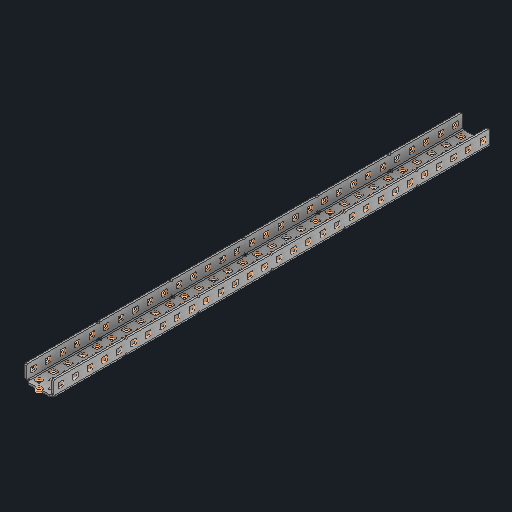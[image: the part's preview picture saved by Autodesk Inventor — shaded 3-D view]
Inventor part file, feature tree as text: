
AUTODESK INVENTOR PART (.ipt)
format: ipt  version: 2025 (Build 290162000, 162)  size: 2,424,832 bytes
history: native  units: in
note: dims shown in document units (in); Inventor stores cm internally (conversion verified against a paired STEP export)
features: other x306, sketch x5, sheet_metal_op x1
ambient origin geometry x8: Origin, YZ Plane, XZ Plane, XY Plane, X Axis, Y Axis, Z Axis, Center Point
bodies: Solid1 (feature_tree)
feature tree (312):
  other  "Alu C 1x2x1x30.ipt"
  other  "Solid1::Alu C 1x2x1x30.ipt"
  other  "TaggingFeature1"
  sketch  "Sketch1"  dims[d0=0.3937in]
  sketch  "Sketch2"  dims[d1=0.0625in]
  sketch  "Sketch3"
  other  "Flange Pattern Sketch"
  sketch  "Sketch9"
  sheet_metal_op  "Body Pattern Sketch"
  other  "Arc Length"
  sketch  "Sketch14"
  other  "Flange Pattern Plane"
  other  "Srf1"
  other  "Srf2"
  other  "Srf3"
  other  "Srf4"
  other  "Srf5"
  other  "Srf6"
  other  "Srf7"
  other  "Srf8"
  other  "Srf9"
  other  "Srf10"
  other  "Srf11"
  other  "Srf12"
  other  "Srf13"
  other  "Srf14"
  other  "Srf15"
  other  "Srf16"
  other  "Srf17"
  other  "Srf18"
  other  "Srf19"
  other  "Srf20"
  other  "Srf21"
  other  "Srf22"
  other  "Srf23"
  other  "Srf24"
  other  "Srf25"
  other  "Srf26"
  other  "Srf27"
  other  "Srf28"
  other  "Srf29"
  other  "Srf30"
  other  "Srf31"
  other  "Srf32"
  other  "Srf33"
  other  "Srf34"
  other  "Srf35"
  other  "Srf36"
  other  "Srf37"
  other  "Srf38"
  other  "Srf39"
  other  "Srf40"
  other  "Srf41"
  other  "Srf42"
  other  "Srf43"
  other  "Srf44"
  other  "Srf45"
  other  "Srf46"
  other  "Srf47"
  other  "Srf48"
  other  "Srf49"
  other  "Srf50"
  other  "Srf51"
  other  "Srf52"
  other  "Srf53"
  other  "Srf54"
  other  "Srf55"
  other  "Srf56"
  other  "Srf57"
  other  "Srf58"
  other  "Srf59"
  other  "Srf60"
  other  "Srf61"
  other  "Srf62"
  other  "Srf63"
  other  "Srf64"
  other  "Srf65"
  other  "Srf66"
  other  "Srf67"
  other  "Srf68"
  other  "Srf69"
  other  "Srf70"
  other  "Srf71"
  other  "Srf72"
  other  "Srf73"
  other  "Srf74"
  other  "Srf75"
  other  "Srf76"
  other  "Srf77"
  other  "Srf78"
  other  "Srf79"
  other  "Srf80"
  other  "Srf81"
  other  "Srf82"
  other  "Srf83"
  other  "Srf84"
  other  "Srf85"
  other  "Srf86"
  other  "Srf87"
  other  "Srf88"
  other  "Srf89"
  other  "Srf90"
  other  "Srf91"
  other  "Srf92"
  other  "Srf93"
  other  "Srf94"
  other  "Srf95"
  other  "Srf96"
  other  "Srf97"
  other  "Srf98"
  other  "Srf99"
  other  "Srf100"
  other  "Srf101"
  other  "Srf102"
  other  "Srf103"
  other  "Srf104"
  other  "Srf105"
  other  "Srf106"
  other  "Srf107"
  other  "Srf108"
  other  "Srf109"
  other  "Srf110"
  other  "Srf111"
  other  "Srf112"
  other  "Srf113"
  other  "Srf114"
  other  "Srf115"
  other  "Srf116"
  other  "Srf117"
  other  "Srf118"
  other  "Srf119"
  other  "Srf120"
  other  "Srf121"
  other  "Srf122"
  other  "Srf123"
  other  "Srf124"
  other  "Srf125"
  other  "Srf126"
  other  "Srf127"
  other  "Srf128"
  other  "Srf129"
  other  "Srf130"
  other  "Srf131"
  other  "Srf132"
  other  "Srf133"
  other  "Srf134"
  other  "Srf135"
  other  "Srf136"
  other  "Srf137"
  other  "Srf138"
  other  "Srf139"
  other  "Srf140"
  other  "Srf141"
  other  "Srf142"
  other  "Srf143"
  other  "Srf144"
  other  "Srf145"
  other  "Srf146"
  other  "Srf147"
  other  "Srf148"
  other  "Srf149"
  other  "Srf150"
  other  "Srf1::Derived"
  other  "Srf2::Derived"
  other  "Srf823::Derived"
  other  "Srf824::Derived"
  other  "Srf825::Derived"
  other  "Srf826::Derived"
  other  "Srf827::Derived"
  other  "Srf828::Derived"
  other  "Srf829::Derived"
  other  "Srf922::Derived"
  other  "Srf923::Derived"
  other  "Srf924::Derived"
  other  "Srf925::Derived"
  other  "Srf926::Derived"
  other  "Srf1143::Derived"
  other  "Srf1144::Derived"
  other  "Srf1145::Derived"
  other  "Srf1146::Derived"
  other  "Srf1147::Derived"
  other  "Srf1148::Derived"
  other  "Srf1149::Derived"
  other  "Srf1150::Derived"
  other  "Srf1151::Derived"
  other  "Srf1152::Derived"
  other  "Srf1153::Derived"
  other  "Srf1154::Derived"
  other  "Srf1155::Derived"
  other  "Srf1156::Derived"
  other  "Srf1157::Derived"
  other  "Srf1158::Derived"
  other  "Srf1159::Derived"
  other  "Srf1160::Derived"
  other  "Srf1161::Derived"
  other  "Srf1162::Derived"
  other  "Srf1163::Derived"
  other  "Srf1164::Derived"
  other  "Srf1165::Derived"
  other  "Srf1166::Derived"
  other  "Srf1167::Derived"
  other  "Srf1168::Derived"
  other  "Srf1169::Derived"
  other  "Srf1170::Derived"
  other  "Srf1171::Derived"
  other  "Srf1172::Derived"
  other  "Srf1173::Derived"
  other  "Srf1174::Derived"
  other  "Srf1175::Derived"
  other  "Srf1176::Derived"
  other  "Srf1177::Derived"
  other  "Srf1178::Derived"
  other  "Srf1179::Derived"
  other  "Srf1180::Derived"
  other  "Srf1181::Derived"
  other  "Srf1182::Derived"
  other  "Srf1183::Derived"
  other  "Srf1184::Derived"
  other  "Srf1185::Derived"
  other  "Srf1186::Derived"
  other  "Srf1187::Derived"
  other  "Srf1188::Derived"
  other  "Srf91::Derived"
  other  "Srf92::Derived"
  other  "Srf856::Derived"
  other  "Srf857::Derived"
  other  "Srf858::Derived"
  other  "Srf859::Derived"
  other  "Srf860::Derived"
  other  "Srf861::Derived"
  other  "Srf862::Derived"
  other  "Srf959::Derived"
  other  "Srf960::Derived"
  other  "Srf961::Derived"
  other  "Srf962::Derived"
  other  "Srf963::Derived"
  other  "Srf1199::Derived"
  other  "Srf1200::Derived"
  other  "Srf1201::Derived"
  other  "Srf1202::Derived"
  other  "Srf1203::Derived"
  other  "Srf1204::Derived"
  other  "Srf1205::Derived"
  other  "Srf1206::Derived"
  other  "Srf1207::Derived"
  other  "Srf1208::Derived"
  other  "Srf1209::Derived"
  other  "Srf1210::Derived"
  other  "Srf1211::Derived"
  other  "Srf1212::Derived"
  other  "Srf1213::Derived"
  other  "Srf1214::Derived"
  other  "Srf1215::Derived"
  other  "Srf1216::Derived"
  other  "Srf1217::Derived"
  other  "Srf1218::Derived"
  other  "Srf1219::Derived"
  other  "Srf1220::Derived"
  other  "Srf1221::Derived"
  other  "Srf1222::Derived"
  other  "Srf1223::Derived"
  other  "Srf1224::Derived"
  other  "Srf1225::Derived"
  other  "Srf1226::Derived"
  other  "Srf1227::Derived"
  other  "Srf1228::Derived"
  other  "Srf1229::Derived"
  other  "Srf1230::Derived"
  other  "Srf1231::Derived"
  other  "Srf1232::Derived"
  other  "Srf1233::Derived"
  other  "Srf1234::Derived"
  other  "Srf1235::Derived"
  other  "Srf1236::Derived"
  other  "Srf1237::Derived"
  other  "Srf1238::Derived"
  other  "Srf1239::Derived"
  other  "Srf1240::Derived"
  other  "Srf1241::Derived"
  other  "Srf1242::Derived"
  other  "Srf1243::Derived"
  other  "Srf1244::Derived"
  other  "Srf786::Derived"
  other  "Srf889::Derived"
  other  "Srf890::Derived"
  other  "Srf891::Derived"
  other  "Srf892::Derived"
  other  "Srf893::Derived"
  other  "Srf894::Derived"
  other  "Srf895::Derived"
  other  "Srf896::Derived"
  other  "Srf996::Derived"
  other  "Srf997::Derived"
  other  "Srf998::Derived"
  other  "Srf999::Derived"
  other  "Srf1000::Derived"
  other  "Srf1255::Derived"
  other  "Srf1256::Derived"
  other  "Srf1257::Derived"
  other  "Srf1258::Derived"
  other  "Srf1259::Derived"
  other  "Srf1260::Derived"
  other  "Srf1261::Derived"
  other  "Srf1262::Derived"
  other  "Srf1263::Derived"
  other  "Srf1264::Derived"
  other  "Srf1265::Derived"
  other  "Srf1266::Derived"
  other  "Srf1267::Derived"
  other  "Srf1268::Derived"
  other  "Srf1269::Derived"
  other  "Srf1270::Derived"
